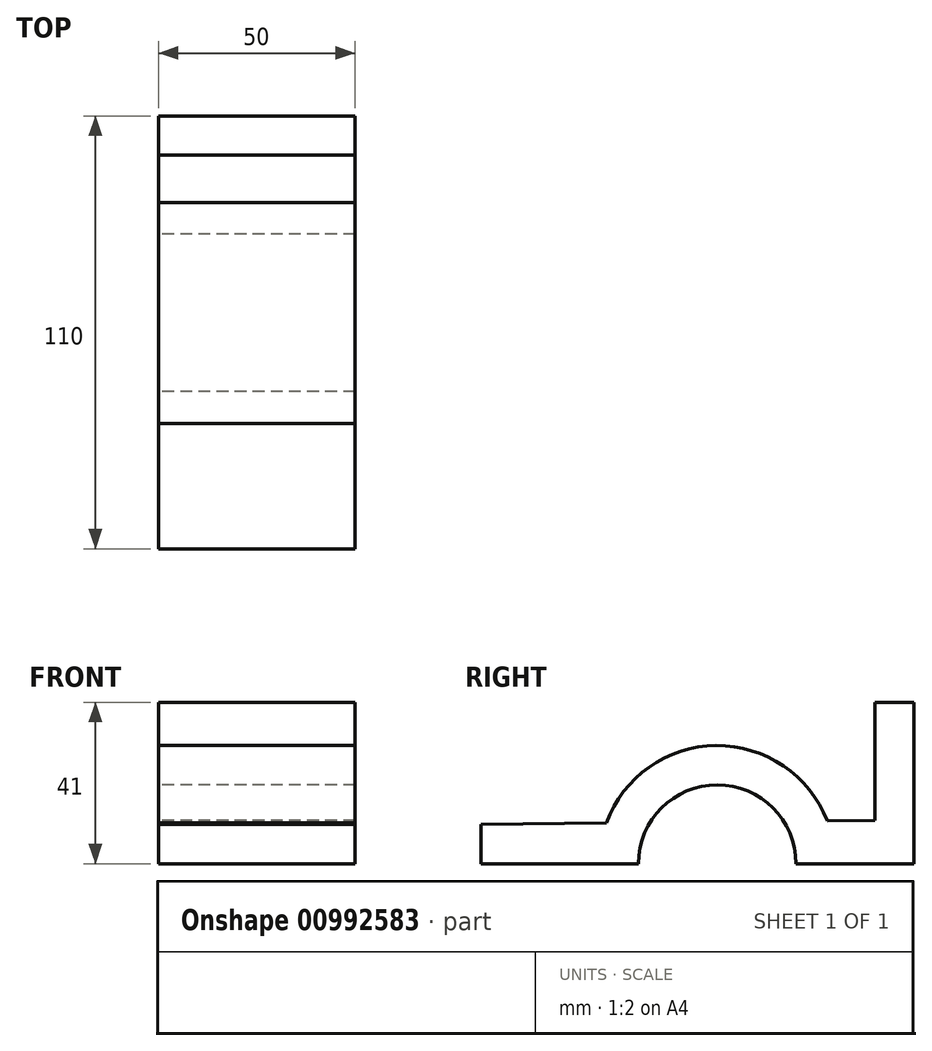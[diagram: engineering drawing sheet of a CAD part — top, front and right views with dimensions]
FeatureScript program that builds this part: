
annotation { "Feature Type Name" : "Feature", "Feature Type Description" : "" }
export const myFeature = defineFeature(function(context is Context, id is Id, definition is map)
    precondition{}
    {
        {
            var Q0;
            Q0=qCreatedBy(makeId("Right.planeOp"),FACE);
            var sketch = newSketch(context, id + "F0", { "sketchPlane" : qUnion([Q0])});
            skLineSegment(sketch, "E0", {"start": v(50, 0) * mm, "end": v(50, 41) * mm});
            skLineSegment(sketch, "E1", {"start": v(50, 41) * mm, "end": v(40, 41) * mm});
            skLineSegment(sketch, "E2", {"start": v(40, 41) * mm, "end": v(40, 11) * mm});
            skLineSegment(sketch, "E3", {"start": v(-60, 0) * mm, "end": v(-60, 10) * mm});
            skLineSegment(sketch, "E4", {"start": v(-60, 10) * mm, "end": v(-28.17, 10.32) * mm});
            skLineSegment(sketch, "E5", {"start": v(-28.17, 10.32) * mm, "end": v(-28.17, 10.32) * mm});
            skArc(sketch, "E6", {"start": v(27.96, 10.88) * mm, "mid": v(-0.3, 30) * mm, "end": v(-28.17, 10.32) * mm});
            skLineSegment(sketch, "E7", {"start": v(27.96, 10.88) * mm, "end": v(40, 11) * mm});
            skLineSegment(sketch, "E8", {"start": v(27.96, 10.88) * mm, "end": v(27.96, 10.88) * mm});
            skPoint(sketch, "E9.start.orphan", {"position": v(-30, 0) * mm});
            skLineSegment(sketch, "E10", {"start": v(-60, 0) * mm, "end": v(-20, 0) * mm});
            skArc(sketch, "E11", {"start": v(20, 0) * mm, "mid": v(0, 20) * mm, "end": v(-20, 0) * mm});
            skLineSegment(sketch, "E12.trimOffspring", {"start": v(20, 0) * mm, "end": v(50, 0) * mm});
            skSolve(sketch);
        }
        {
            var Q0;
            Q0=makeQuery(id+"F0.imprint","IMPRINT",FACE,{"disambiguationData":[TD([[makeQuery(id+"F0.imprint","IMPRINT",EDGE,{"derivedFrom":sQuery(id+"F0.wireOp",EDGE,"E0")}),1.0]])]});
            var Q1;
            Q1 = qSketchRegion(id + "F2", true);
            extrude(context, id + "F1", {"entities" : qUnion([Q0, Q1]), "depth" : 50 * mm, "offsetDistance" : 25 * mm});
        }
    });
